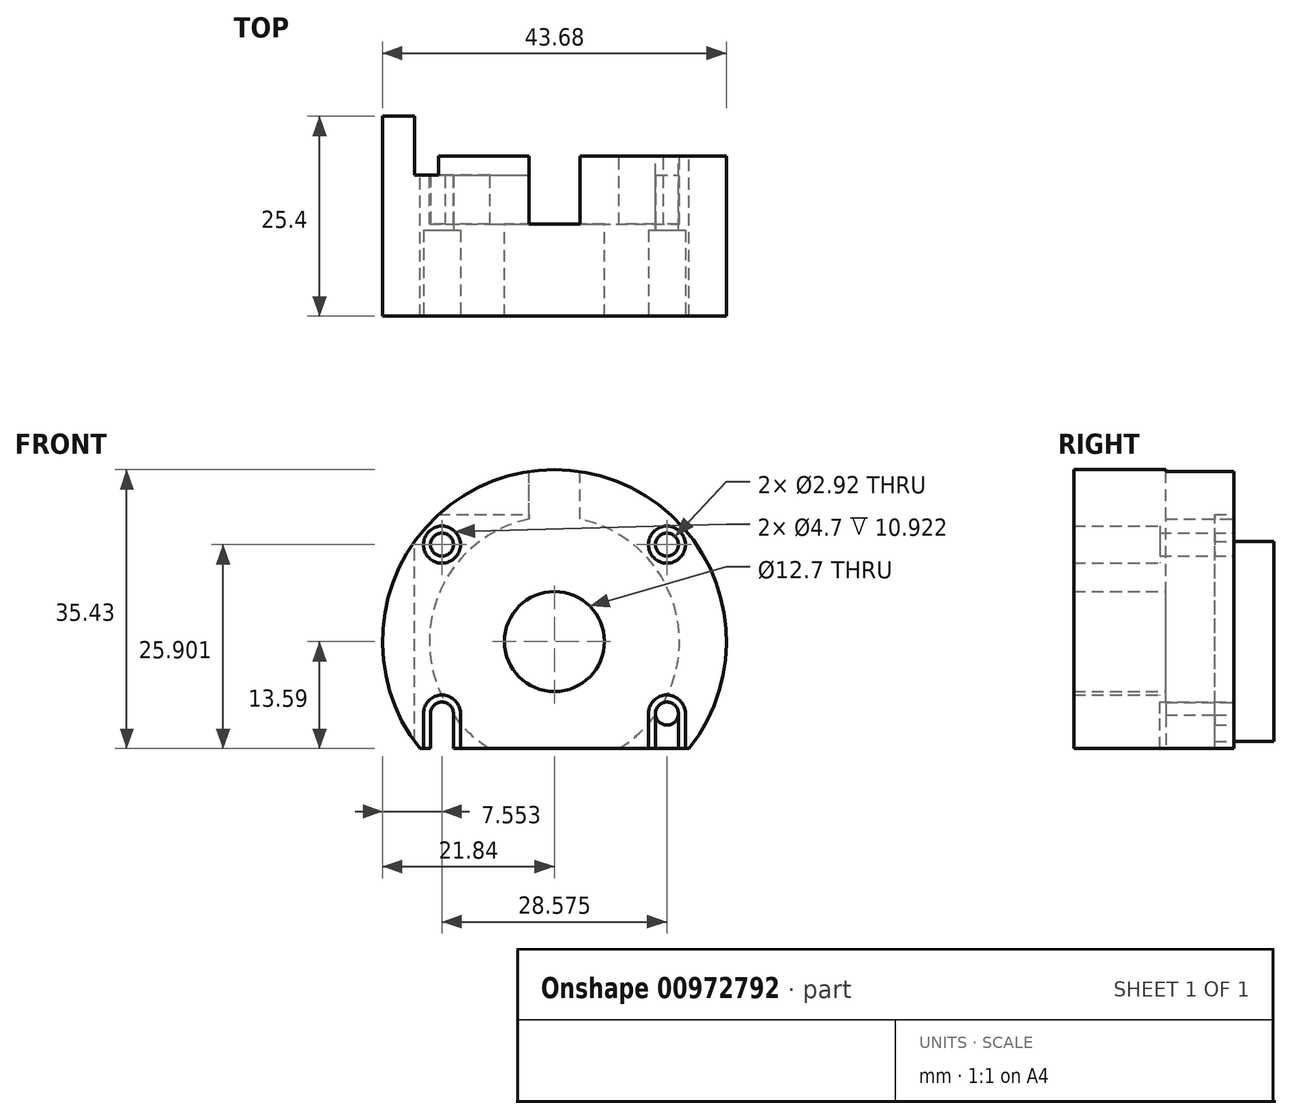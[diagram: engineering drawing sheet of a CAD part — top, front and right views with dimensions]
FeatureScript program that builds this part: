
annotation { "Feature Type Name" : "Feature", "Feature Type Description" : "" }
export const myFeature = defineFeature(function(context is Context, id is Id, definition is map)
    precondition{}
    {
        {
            var Q0;
            Q0=qCreatedBy(makeId("Front.planeOp"),FACE);
            var sketch = newSketch(context, id + "F0", { "sketchPlane" : qUnion([Q0])});
            skArc(sketch, "E0", {"start": v(17.1, -13.59) * mm, "mid": v(0, 21.84) * mm, "end": v(-17.1, -13.59) * mm});
            skCircle(sketch, "E1", {"center": v(0, 0) * mm, "radius": 6.35 * mm});
            skLineSegment(sketch, "E2", {"start": v(0, -13.59) * mm, "end": v(-17.1, -13.59) * mm});
            skLineSegment(sketch, "E3", {"start": v(0, -13.59) * mm, "end": v(17.1, -13.59) * mm});
            skSolve(sketch);
        }
        {
            var Q0;
            Q0=makeQuery(id+"F0.imprint","IMPRINT",FACE,{"disambiguationData":[TD([[makeQuery(id+"F0.imprint","IMPRINT",EDGE,{"derivedFrom":sQuery(id+"F0.wireOp",EDGE,"E0")}),1.0]])]});
            extrude(context, id + "F1", {"entities" : qUnion([Q0]), "depth" : 25.4 * mm, "offsetDistance" : 25.4 * mm});
        }
        {
            var Q0;
            Q0=makeQuery(id+"F1.opExtrude","CAP_FACE",FACE,{"disambiguationData":[OSD([sQuery(id+"F0.wireOp",EDGE,"E0"),sQuery(id+"F0.wireOp",EDGE,"E1"),sQuery(id+"F0.wireOp",EDGE,"E2"),sQuery(id+"F0.wireOp",EDGE,"E3")])],"isStart":true});
            var sketch = newSketch(context, id + "F2", { "sketchPlane" : qUnion([Q0])});
            skArc(sketch, "E4", {"start": v(-3.25, 15.54) * mm, "mid": v(0, -15.88) * mm, "end": v(3.25, 15.54) * mm});
            skArc(sketch, "E5", {"start": v(3.25, 21.6) * mm, "mid": v(0, 21.84) * mm, "end": v(-3.25, 21.6) * mm, "construction": true});
            skLineSegment(sketch, "E6.0", {"start": v(3.25, 15.54) * mm, "end": v(3.25, 21.6) * mm});
            skLineSegment(sketch, "E7.0", {"start": v(-3.25, 15.54) * mm, "end": v(-3.25, 21.6) * mm});
            skSolve(sketch);
        }
        {
            var Q0;
            {var subQ1=sQuery(id+"F2.wireOp",EDGE,"E6.0");Q0=makeQuery(id+"F2.imprint","IMPRINT",FACE,{"disambiguationData":[TD([[makeQuery(id+"F2.imprint","IMPRINT",EDGE,{"derivedFrom":subQ1}),1.0]])]});}
            extrude(context, id + "F3", {"entities" : qUnion([Q0]), "operationType" : NewBodyOperationType.REMOVE, "oppositeDirection" : true, "depth" : 13.72 * mm, "offsetDistance" : 25.4 * mm});
        }
        {
            var Q0;
            {var subQ0=sQuery(id+"F0.wireOp",EDGE,"E0");var subQ1=sQuery(id+"F0.wireOp",EDGE,"E3");var subQ2=sQuery(id+"F0.wireOp",EDGE,"E2");var subQ3=sQuery(id+"F2.wireOp",EDGE,"E7.0");Q0=makeQuery(id+"F3.boolean.opBoolean","SPLIT",FACE,{"disambiguationData":[TD([makeQuery(id+"F3.opExtrude","SWEPT_FACE",FACE,{"disambiguationData":[OSD([subQ3])]})])],"derivedFrom":makeQuery(id+"F1.opExtrude","CAP_FACE",FACE,{"disambiguationData":[OSD([subQ0,sQuery(id+"F0.wireOp",EDGE,"E1"),subQ2,subQ1])],"isStart":true})});}
            var sketch = newSketch(context, id + "F4", { "sketchPlane" : qUnion([Q0])});
            skLineSegment(sketch, "E8", {"start": v(0, -13.59) * mm, "end": v(17.78, -13.59) * mm});
            skLineSegment(sketch, "E9", {"start": v(17.78, -13.59) * mm, "end": v(17.78, 16.13) * mm});
            skLineSegment(sketch, "E10", {"start": v(17.78, 16.13) * mm, "end": v(-17.78, 16.13) * mm});
            skLineSegment(sketch, "E11", {"start": v(-17.78, 16.13) * mm, "end": v(-17.78, -13.59) * mm});
            skLineSegment(sketch, "E12", {"start": v(0, -13.59) * mm, "end": v(-17.78, -13.59) * mm});
            skSolve(sketch);
        }
        {
            var Q0;
            {var subQ0=sQuery(id+"F2.wireOp",EDGE,"E7.0");var subQ1=sQuery(id+"F2.wireOp",EDGE,"E4");var subQ4=makeQuery(id+"F3.boolean.opBoolean","COPY",EDGE,{"derivedFrom":makeQuery(id+"F3.opExtrude","CAP_EDGE",EDGE,{"disambiguationData":[OSD([subQ1]),TDD([makeQuery(id+"F2.imprint","IMPRINT",EDGE,{"disambiguationData":[TD([[makeQuery(id+"F2.imprint","INTERSECT",VERTEX,{"derivedFrom":[subQ1,subQ0]}),-1.0]])],"derivedFrom":subQ1})])],"isStart":true})});Q0=makeQuery(id+"F4.imprint","IMPRINT",FACE,{"disambiguationData":[TD([[makeQuery(id+"F4.imprint","IMPRINT",EDGE,{"derivedFrom":subQ4}),-1.0]])]});}
            var Q1;
            {var subQ4=sQuery(id+"F4.wireOp",EDGE,"E8");Q1=makeQuery(id+"F4.imprint","IMPRINT",FACE,{"disambiguationData":[TD([[makeQuery(id+"F4.imprint","IMPRINT",EDGE,{"derivedFrom":subQ4}),1.0]])]});}
            extrude(context, id + "F5", {"entities" : qUnion([Q0, Q1]), "operationType" : NewBodyOperationType.REMOVE, "oppositeDirection" : true, "depth" : 7.5 * mm, "offsetDistance" : 25.4 * mm});
        }
        {
            var Q0;
            {var subQ0=sQuery(id+"F0.wireOp",EDGE,"E0");var subQ2=sQuery(id+"F2.wireOp",EDGE,"E7.0");var subQ3=makeQuery(id+"F3.opExtrude","SWEPT_FACE",FACE,{"disambiguationData":[OSD([subQ2])]});var subQ4=sQuery(id+"F0.wireOp",EDGE,"E3");var subQ5=sQuery(id+"F0.wireOp",EDGE,"E2");Q0=makeQuery(id+"F5.boolean.opBoolean","SPLIT",FACE,{"disambiguationData":[TD([makeQuery(id+"F3.boolean.opBoolean","COPY",FACE,{"derivedFrom":subQ3})])],"derivedFrom":makeQuery(id+"F3.boolean.opBoolean","SPLIT",FACE,{"disambiguationData":[TD([subQ3])],"derivedFrom":makeQuery(id+"F1.opExtrude","CAP_FACE",FACE,{"disambiguationData":[OSD([subQ0,sQuery(id+"F0.wireOp",EDGE,"E1"),subQ5,subQ4])],"isStart":true})})});}
            var Q1;
            {var subQ0=sQuery(id+"F0.wireOp",EDGE,"E0");var subQ2=sQuery(id+"F2.wireOp",EDGE,"E6.0");var subQ3=makeQuery(id+"F3.opExtrude","SWEPT_FACE",FACE,{"disambiguationData":[OSD([subQ2])]});var subQ4=sQuery(id+"F0.wireOp",EDGE,"E3");var subQ5=sQuery(id+"F0.wireOp",EDGE,"E2");Q1=makeQuery(id+"F5.boolean.opBoolean","SPLIT",FACE,{"disambiguationData":[TD([makeQuery(id+"F3.boolean.opBoolean","COPY",FACE,{"derivedFrom":subQ3})])],"derivedFrom":makeQuery(id+"F3.boolean.opBoolean","SPLIT",FACE,{"disambiguationData":[TD([subQ3])],"derivedFrom":makeQuery(id+"F1.opExtrude","CAP_FACE",FACE,{"disambiguationData":[OSD([subQ0,sQuery(id+"F0.wireOp",EDGE,"E1"),subQ5,subQ4])],"isStart":true})})});}
            extrude(context, id + "F6", {"entities" : qUnion([Q0, Q1]), "operationType" : NewBodyOperationType.REMOVE, "oppositeDirection" : true, "depth" : 5.08 * mm, "offsetDistance" : 25.4 * mm});
        }
        {
            var Q0;
            Q0=makeQuery(id+"F1.opExtrude","CAP_FACE",FACE,{"disambiguationData":[OSD([sQuery(id+"F0.wireOp",EDGE,"E0"),sQuery(id+"F0.wireOp",EDGE,"E1"),sQuery(id+"F0.wireOp",EDGE,"E2"),sQuery(id+"F0.wireOp",EDGE,"E3")])],"isStart":false});
            var sketch = newSketch(context, id + "F7", { "sketchPlane" : qUnion([Q0])});
            skPoint(sketch, "E13", {"position": v(-14.29, 12.31) * mm});
            skPoint(sketch, "E14", {"position": v(14.29, 12.31) * mm});
            skPoint(sketch, "E15", {"position": v(14.29, -9.15) * mm});
            skPoint(sketch, "E16", {"position": v(-14.29, -9.15) * mm});
            skArc(sketch, "E17", {"start": v(15.75, -9.15) * mm, "mid": v(14.29, -7.7) * mm, "end": v(12.83, -9.15) * mm});
            skArc(sketch, "E18", {"start": v(16.64, -9.15) * mm, "mid": v(14.29, -6.8) * mm, "end": v(11.94, -9.15) * mm});
            skArc(sketch, "E19", {"start": v(-12.83, -9.15) * mm, "mid": v(-14.29, -7.7) * mm, "end": v(-15.75, -9.15) * mm});
            skArc(sketch, "E20", {"start": v(-11.94, -9.15) * mm, "mid": v(-14.29, -6.8) * mm, "end": v(-16.64, -9.15) * mm});
            skLineSegment(sketch, "E21.0", {"start": v(16.64, -13.59) * mm, "end": v(16.64, -9.15) * mm});
            skLineSegment(sketch, "E22.0", {"start": v(11.94, -13.59) * mm, "end": v(11.94, -9.15) * mm});
            skLineSegment(sketch, "E23.0", {"start": v(15.75, -13.59) * mm, "end": v(15.75, -9.15) * mm});
            skLineSegment(sketch, "E24.0", {"start": v(12.83, -13.59) * mm, "end": v(12.83, -9.15) * mm});
            skLineSegment(sketch, "E25.0", {"start": v(-12.83, -13.59) * mm, "end": v(-12.83, -9.15) * mm});
            skLineSegment(sketch, "E26.0", {"start": v(-15.75, -13.59) * mm, "end": v(-15.75, -9.15) * mm});
            skLineSegment(sketch, "E27.0", {"start": v(-11.94, -13.59) * mm, "end": v(-11.94, -9.15) * mm});
            skLineSegment(sketch, "E28.0", {"start": v(-13.7, -7.24) * mm, "end": v(13.7, -7.24) * mm});
            skArc(sketch, "E28.1", {"start": v(13.7, -7.24) * mm, "mid": v(0, 15.5) * mm, "end": v(-13.7, -7.24) * mm});
            skLineSegment(sketch, "E29.0", {"start": v(-16.64, -13.59) * mm, "end": v(-16.64, -9.15) * mm});
            skSolve(sketch);
        }
        {
            var Q0;
            Q0=sQuery(id+"F7.wireOp",VERTEX,"E16");
            var Q1;
            Q1=sQuery(id+"F7.wireOp",VERTEX,"E13");
            var Q2;
            Q2=sQuery(id+"F7.wireOp",VERTEX,"E14");
            var Q3;
            Q3=sQuery(id+"F7.wireOp",VERTEX,"E15");
            var Q4;
            Q4=makeQuery(id+"F1.opExtrude","SWEPT_BODY",BODY,{"disambiguationData":[OSD([sQuery(id+"F0.wireOp",EDGE,"E0"),sQuery(id+"F0.wireOp",EDGE,"E1"),sQuery(id+"F0.wireOp",EDGE,"E2"),sQuery(id+"F0.wireOp",EDGE,"E3")])]});
            hole(context, id + "F8", {"style" : HoleStyle.C_BORE, "endStyle" : HoleEndStyle.THROUGH, "holeDiameter" : 2.92 * mm, "cBoreDiameter" : 4.7 * mm, "cBoreDepth" : 10.92 * mm, "majorDiameter" : 4.83 * mm, "isTappedThrough" : true, "tappedDepth" : 9.52 * mm, "tapClearance" : 3, "locations" : qUnion([Q0, Q1, Q2, Q3]), "scope" : qUnion([Q4]), "startStyle" : HoleStartStyle.PART});
        }
        {
            var Q0;
            Q0=makeQuery(id+"F7.imprint","IMPRINT",FACE,{"disambiguationData":[TD([[makeQuery(id+"F7.imprint","IMPRINT",EDGE,{"derivedFrom":sQuery(id+"F7.wireOp",EDGE,"E19")}),-1.0]])]});
            var Q1;
            Q1=makeQuery(id+"F7.imprint","IMPRINT",FACE,{"disambiguationData":[TD([[makeQuery(id+"F7.imprint","IMPRINT",EDGE,{"derivedFrom":sQuery(id+"F7.wireOp",EDGE,"E17")}),-1.0]])]});
            extrude(context, id + "F9", {"entities" : qUnion([Q0, Q1]), "operationType" : NewBodyOperationType.REMOVE, "oppositeDirection" : true, "depth" : 10.92 * mm, "offsetDistance" : 25.4 * mm});
        }
        {
            var Q0;
            Q0=makeQuery(id+"F7.imprint","IMPRINT",FACE,{"disambiguationData":[TD([[makeQuery(id+"F7.imprint","IMPRINT",EDGE,{"derivedFrom":sQuery(id+"F7.wireOp",EDGE,"E19")}),1.0]])]});
            var Q1;
            Q1=makeQuery(id+"F7.imprint","IMPRINT",FACE,{"disambiguationData":[TD([[makeQuery(id+"F7.imprint","IMPRINT",EDGE,{"derivedFrom":sQuery(id+"F7.wireOp",EDGE,"E17")}),1.0]])]});
            extrude(context, id + "F10", {"entities" : qUnion([Q0, Q1]), "operationType" : NewBodyOperationType.REMOVE, "oppositeDirection" : true, "depth" : 17.9 * mm, "offsetDistance" : 25.4 * mm});
        }
    });
